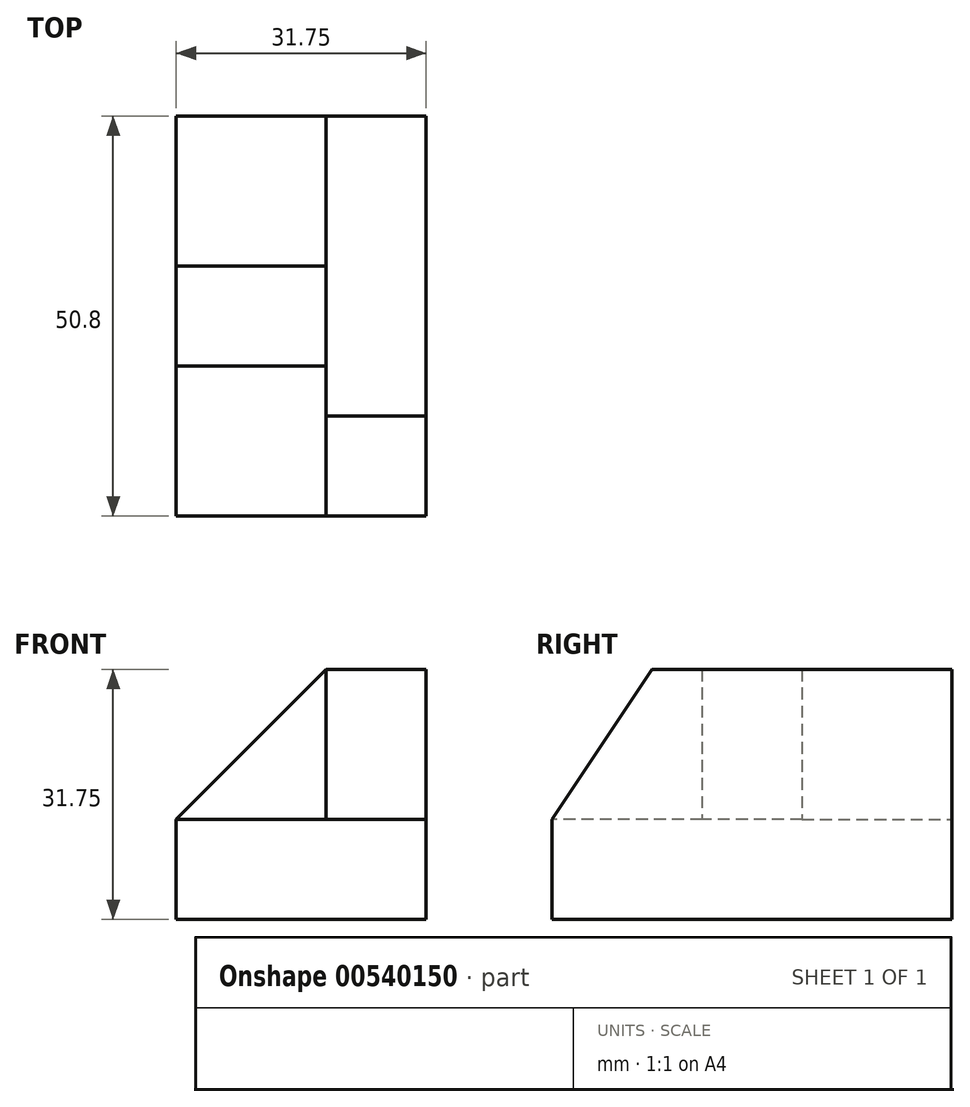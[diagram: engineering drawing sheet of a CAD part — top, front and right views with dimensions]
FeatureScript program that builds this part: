
annotation { "Feature Type Name" : "Feature", "Feature Type Description" : "" }
export const myFeature = defineFeature(function(context is Context, id is Id, definition is map)
    precondition{}
    {
        {
            var Q0;
            Q0=qCreatedBy(makeId("Front.planeOp"),FACE);
            var sketch = newSketch(context, id + "F0", { "sketchPlane" : qUnion([Q0])});
            skLineSegment(sketch, "E0", {"start": v(5.72, 38.06) * mm, "end": v(21.3, 38.06) * mm});
            skLineSegment(sketch, "E1", {"start": v(21.3, 38.06) * mm, "end": v(21.3, 6.3) * mm});
            skLineSegment(sketch, "E2", {"start": v(21.3, 6.3) * mm, "end": v(-10.45, 6.3) * mm});
            skLineSegment(sketch, "E3", {"start": v(-10.45, 6.3) * mm, "end": v(-10.45, 38.06) * mm});
            skLineSegment(sketch, "E4", {"start": v(-10.45, 38.06) * mm, "end": v(5.72, 38.06) * mm});
            skSolve(sketch);
        }
        {
            var Q0;
            Q0 = qSketchRegion(id + "F0", true);
            var Q1;
            Q1 = qSketchRegion(id + "F3", true);
            extrude(context, id + "F1", {"entities" : qUnion([Q0, Q1]), "depth" : 50.8 * mm, "offsetDistance" : 25.4 * mm});
        }
        {
            var Q0;
            Q0=makeQuery(id+"F1.opExtrude","CAP_FACE",FACE,{"disambiguationData":[OSD([sQuery(id+"F0.wireOp",EDGE,"E0"),sQuery(id+"F0.wireOp",EDGE,"E1"),sQuery(id+"F0.wireOp",EDGE,"E2"),sQuery(id+"F0.wireOp",EDGE,"E3"),sQuery(id+"F0.wireOp",EDGE,"E4")])],"isStart":false});
            var sketch = newSketch(context, id + "F2", { "sketchPlane" : qUnion([Q0])});
            skLineSegment(sketch, "E5", {"start": v(8.6, 38.06) * mm, "end": v(8.6, 19) * mm});
            skLineSegment(sketch, "E6", {"start": v(-10.45, 19) * mm, "end": v(8.6, 19) * mm});
            skSolve(sketch);
        }
        {
            var Q0;
            Q0=makeQuery(id+"F1.opExtrude","SWEPT_FACE",FACE,{"disambiguationData":[OSD([sQuery(id+"F0.wireOp",EDGE,"E1")])]});
            var sketch = newSketch(context, id + "F3", { "sketchPlane" : qUnion([Q0])});
            skLineSegment(sketch, "E7", {"start": v(-50.8, 19) * mm, "end": v(-38.1, 38.06) * mm});
            skSolve(sketch);
        }
        {
            var Q0;
            {var subQ0=sQuery(id+"F3.wireOp",EDGE,"E7");Q0=makeQuery(id+"F3.imprint","IMPRINT",FACE,{"disambiguationData":[TD([[makeQuery(id+"F3.imprint","IMPRINT",EDGE,{"derivedFrom":subQ0}),1.0]])]});}
            extrude(context, id + "F4", {"entities" : qUnion([Q0]), "operationType" : NewBodyOperationType.REMOVE, "oppositeDirection" : true, "depth" : 12.7 * mm, "offsetDistance" : 25.4 * mm});
        }
        {
            var Q0;
            {var subQ0=sQuery(id+"F2.wireOp",EDGE,"E5");Q0=makeQuery(id+"F2.imprint","IMPRINT",FACE,{"disambiguationData":[TD([[makeQuery(id+"F2.imprint","IMPRINT",EDGE,{"derivedFrom":subQ0}),-1.0]])]});}
            extrude(context, id + "F5", {"entities" : qUnion([Q0]), "operationType" : NewBodyOperationType.REMOVE, "oppositeDirection" : true, "depth" : 19.05 * mm, "offsetDistance" : 25.4 * mm});
        }
        {
            var Q0;
            Q0=makeQuery(id+"F5.boolean.opBoolean","COPY",FACE,{"derivedFrom":makeQuery(id+"F5.opExtrude","CAP_FACE",FACE,{"disambiguationData":[OSD([sQuery(id+"F0.wireOp",EDGE,"E0"),sQuery(id+"F0.wireOp",EDGE,"E3"),sQuery(id+"F0.wireOp",EDGE,"E4"),sQuery(id+"F2.wireOp",EDGE,"E5"),sQuery(id+"F2.wireOp",EDGE,"E6")])],"isStart":false})});
            var sketch = newSketch(context, id + "F6", { "sketchPlane" : qUnion([Q0])});
            skLineSegment(sketch, "E8", {"start": v(8.6, 38.06) * mm, "end": v(-10.45, 19) * mm});
            skSolve(sketch);
        }
        {
            var Q0;
            Q0=makeQuery(id+"F6.imprint","IMPRINT",FACE,{"disambiguationData":[TD([[makeQuery(id+"F6.imprint","IMPRINT",EDGE,{"derivedFrom":sQuery(id+"F6.wireOp",EDGE,"E8")}),-1.0]])]});
            extrude(context, id + "F7", {"entities" : qUnion([Q0]), "operationType" : NewBodyOperationType.REMOVE, "oppositeDirection" : true, "depth" : 12.7 * mm, "offsetDistance" : 25.4 * mm});
        }
        {
            var Q0;
            Q0=makeQuery(id+"F1.opExtrude","CAP_FACE",FACE,{"disambiguationData":[OSD([sQuery(id+"F0.wireOp",EDGE,"E0"),sQuery(id+"F0.wireOp",EDGE,"E1"),sQuery(id+"F0.wireOp",EDGE,"E2"),sQuery(id+"F0.wireOp",EDGE,"E3"),sQuery(id+"F0.wireOp",EDGE,"E4")])],"isStart":true});
            var sketch = newSketch(context, id + "F8", { "sketchPlane" : qUnion([Q0])});
            skLineSegment(sketch, "E9", {"start": v(-8.6, 38.06) * mm, "end": v(-8.6, 19) * mm});
            skLineSegment(sketch, "E10", {"start": v(-8.6, 19) * mm, "end": v(10.45, 19) * mm});
            skSolve(sketch);
        }
        {
            var Q0;
            {var subQ0=sQuery(id+"F8.wireOp",EDGE,"E9");Q0=makeQuery(id+"F8.imprint","IMPRINT",FACE,{"disambiguationData":[TD([[makeQuery(id+"F8.imprint","IMPRINT",EDGE,{"derivedFrom":subQ0}),1.0]])]});}
            extrude(context, id + "F9", {"entities" : qUnion([Q0]), "operationType" : NewBodyOperationType.REMOVE, "oppositeDirection" : true, "depth" : 19.05 * mm, "offsetDistance" : 25.4 * mm});
        }
    });
